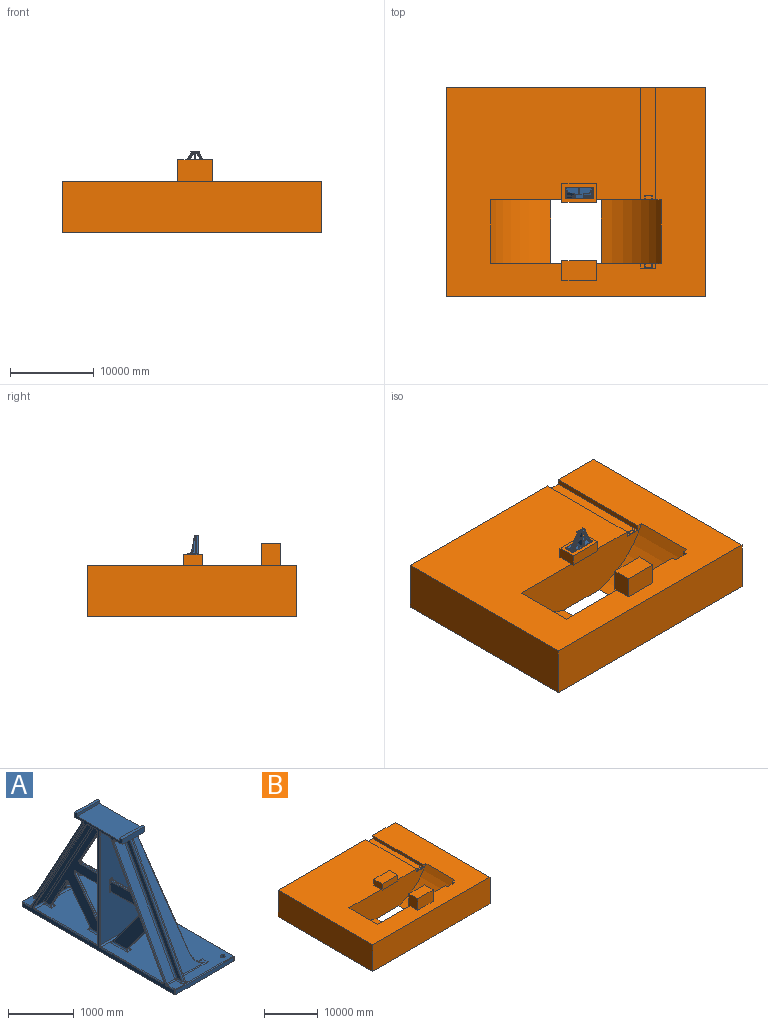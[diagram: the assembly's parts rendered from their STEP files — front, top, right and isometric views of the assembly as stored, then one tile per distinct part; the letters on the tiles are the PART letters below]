
ASSEMBLY  parts=2 mates=1
PART A: 292 faces, bbox 1283.8x3315.8x2337.9 mm
  f0: plane 2082.8x1322.33mm, normal (1,0,0), area 575527.7mm2, adj f52,f55,f57,f65,f122,f123,f124,f125
  f1: plane 2095.5x1322.33mm, normal (-1,0,0), area 576903.3mm2, adj f60,f62,f67,f78,f81,f82,f83,f84
  f2: plane 603.57x326.81mm, normal (0,0.88,-0.48), area 17433.8mm2, adj f58,f72,f98,f139
  f3: plane 3276.6x1244.6mm, normal (0,0,1), area 3608920.8mm2, adj f9,f30,f31,f35,f36,f38,f39,f42
  f4: plane 1020.58x474.48mm, normal (0,0,-1), area 273321.6mm2, adj f10,f12,f14,f29,f33,f41,f44,f45
  f5: plane 1244.6x76.2mm, normal (0,-1,0), area 94838.5mm2, adj f6,f103,f107,f108
  f6: plane 3302x1270mm, normal (0,0,-1), area 4184280.8mm2, adj f5,f7,f8,f103,f108,f150,f154,f244
  f7: plane 3276.6x76.2mm, normal (1,0,0), area 249676.9mm2, adj f6,f102,f103,f244
  f8: plane 3276.6x2324.1mm, normal (-1,0,0), area 478440.9mm2, adj f6,f13,f14,f15,f16,f101,f104,f106
  f9: cylinder r=457.2mm len=450.25mm, axis (0,1,0), area 36318.4mm2, adj f3,f10,f11,f70,f155,f212
  f10: plane 1757.68x311.48mm, normal (0.98,0,0.17), area 90851.4mm2, adj f4,f9,f11,f64,f155,f206
  f11: plane 2096.57x1067.85mm, normal (0,-1,0), area 1321127.4mm2, adj f9,f10,f64,f68,f70,f71,f85,f86
  f12: plane 1016x101.6mm, normal (1,0,0), area 56774.1mm2, adj f4,f13,f14,f15,f16,f156,f157,f158
  f13: plane 482.6x50.8mm, normal (0,0,1), area 24516.1mm2, adj f8,f12,f14,f16
  f14: plane 482.6x101.6mm, normal (0,-1,0), area 48997.5mm2, adj f4,f8,f12,f13,f101
  f15: plane 914.4x482.6mm, normal (0,0,1), area 441289.4mm2, adj f8,f12,f16,f158
  f16: plane 482.6x50.8mm, normal (0,1,0), area 24516.1mm2, adj f8,f12,f13,f15
  f17: plane 2083.01x1127.98mm, normal (0,-0.88,0.48), area 60174.3mm2, adj f19,f35,f38,f45,f46
  f18: plane 952.62x515.81mm, normal (0,0.88,-0.48), area 27546.8mm2, adj f50,f69,f81,f132,f133
  f19: plane 2082.8x1250.53mm, normal (1,0,0), area 255697.1mm2, adj f17,f34,f35,f41,f45
  f20: plane 2082.8x1221.65mm, normal (-1,0,0), area 195521.9mm2, adj f39,f43,f46,f49
  f21: plane 651.4x25.4mm, normal (0,0,-1), area 16545.6mm2, adj f71,f73,f89,f124
  f22: plane 546.03x25.4mm, normal (0,0,1), area 13869.1mm2, adj f68,f69,f83,f130
  f23: plane 869.61x653.2mm, normal (0,0.8,0.6), area 27764.6mm2, adj f73,f74,f91,f92,f121,f122
  f24: plane 603.57x453.37mm, normal (0,-0.8,-0.6), area 19173.9mm2, adj f66,f72,f96,f137
  f25: plane 2082.8x1127.77mm, normal (0,-0.88,0.48), area 421124.2mm2, adj f36,f43,f44,f106
  f26: plane 2082.8x1127.77mm, normal (0,0.88,-0.48), area 421124.2mm2, adj f59,f62,f63,f118
  f27: plane 2082.8x1127.77mm, normal (0,0.88,-0.48), area 592711.8mm2, adj f51,f54,f55,f143,f144
  f28: plane 2082.8x1127.77mm, normal (0,-0.88,0.48), area 604847.9mm2, adj f31,f33,f34,f147,f148
  f29: plane 1901.74x1059.44mm, normal (1,0,0.09), area 55530.4mm2, adj f4,f30,f142,f143,f148,f149
  f30: cylinder r=254mm len=253.03mm, axis (0,1,0), area 16525mm2, adj f3,f29,f144,f145,f146,f147
  f31: cylinder r=25.4mm len=588.35mm, axis (1,0,0), area 14676.3mm2, adj f3,f28,f32,f146
  f32: sphere r=25.4mm, area 494.1mm2, adj f31,f34,f35
  f33: cylinder r=25.4mm len=160mm, axis (1,0,0), area 8271.1mm2, adj f4,f28,f37,f149
  f34: cylinder r=25.4mm len=2094.89mm, axis (0,0.48,0.88), area 94500mm2, adj f19,f28,f32,f37
  f35: cylinder r=25.4mm len=151.64mm, axis (0,-1,0), area 5422.7mm2, adj f3,f17,f19,f32,f38
  f36: cylinder r=25.4mm len=177.8mm, axis (1,0,0), area 4852.7mm2, adj f3,f25,f40,f109
  f37: sphere r=25.4mm, area 1333.6mm2, adj f33,f34,f41
  f38: cylinder r=25.4mm len=50.8mm, axis (1,0,0), area 1081.7mm2, adj f3,f17,f35,f42
  f39: cylinder r=25.4mm len=93.87mm, axis (0,1,0), area 3745.4mm2, adj f3,f20,f40,f42
  f40: sphere r=25.4mm, area 640.7mm2, adj f36,f39,f43
  f41: cylinder r=25.4mm len=151.64mm, axis (0,1,0), area 5543.6mm2, adj f4,f19,f37,f45
  f42: bspline ~60.29x59.63mm, area 2051.8mm2, adj f3,f38,f39,f46
  f43: cylinder r=25.4mm len=2094.89mm, axis (0,-0.48,-0.88), area 94500mm2, adj f20,f25,f40,f47
  f44: cylinder r=25.4mm len=177.8mm, axis (1,0,0), area 9335.1mm2, adj f4,f25,f47,f104
  f45: cylinder r=25.4mm len=50.8mm, axis (1,0,0), area 1840.3mm2, adj f4,f17,f19,f41,f48
  f46: cylinder r=25.4mm len=2119.08mm, axis (0,0.48,0.88), area 94500mm2, adj f17,f20,f42,f48
  f47: sphere r=25.4mm, area 1333.6mm2, adj f43,f44,f49
  f48: bspline ~57.77x50.8mm, area 2732.6mm2, adj f4,f45,f46,f49
  f49: cylinder r=25.4mm len=93.87mm, axis (0,-1,0), area 3745.4mm2, adj f4,f20,f47,f48
  f50: cylinder r=25.4mm len=63.5mm, axis (1,0,0), area 1275.9mm2, adj f4,f18,f79,f134
  f51: cylinder r=25.4mm len=156.82mm, axis (1,0,0), area 4256.3mm2, adj f4,f27,f53,f142
  f52: cylinder r=25.4mm len=151.64mm, axis (0,1,0), area 5108.9mm2, adj f0,f4,f53,f133,f134
  f53: sphere r=25.4mm, area 494.1mm2, adj f51,f52,f55
  f54: cylinder r=25.4mm len=588.35mm, axis (1,0,0), area 26589.8mm2, adj f3,f27,f56,f145
  f55: cylinder r=25.4mm len=2094.89mm, axis (0,-0.48,-0.88), area 94500mm2, adj f0,f27,f53,f56
  f56: sphere r=25.4mm, area 1374.7mm2, adj f54,f55,f57
  f57: cylinder r=25.4mm len=151.64mm, axis (0,-1,0), area 5290.2mm2, adj f0,f3,f56,f141
  f58: cylinder r=25.4mm len=101.6mm, axis (1,0,0), area 2438.4mm2, adj f2,f3,f99,f100,f140,f141
  f59: cylinder r=25.4mm len=177.8mm, axis (1,0,0), area 9335.1mm2, adj f3,f26,f61,f116
  f60: cylinder r=25.4mm len=151.64mm, axis (0,1,0), area 5290.2mm2, adj f1,f3,f61,f100
  f61: sphere r=25.4mm, area 1292.5mm2, adj f59,f60,f62
  f62: cylinder r=25.4mm len=2107.59mm, axis (0,0.48,0.88), area 94813.9mm2, adj f1,f26,f61,f75,f76
  f63: cylinder r=25.4mm len=188.97mm, axis (1,0,0), area 5005.1mm2, adj f4,f26,f75,f119
  f64: cylinder r=25.4mm len=448.98mm, axis (-1,0,0), area 17824.1mm2, adj f4,f10,f11,f115
  f65: cylinder r=25.4mm len=378.52mm, axis (0,1,0), area 13151.4mm2, adj f0,f3,f70,f120,f121,f135
  f66: cylinder r=25.4mm len=101.6mm, axis (1,0,0), area 2949.2mm2, adj f3,f24,f94,f95,f135,f136
  f67: cylinder r=25.4mm len=378.52mm, axis (0,-1,0), area 13151.4mm2, adj f1,f3,f70,f92,f93,f94
  f68: cylinder r=25.4mm len=25.4mm, axis (1,0,0), area 1013.4mm2, adj f11,f22,f84,f129
  f69: cylinder r=25.4mm len=37.49mm, axis (-1,0,0), area 1333.6mm2, adj f18,f22,f82,f131
  f70: cylinder r=25.4mm len=1204.35mm, axis (1,0,0), area 44777.6mm2, adj f3,f9,f11,f65,f67,f74,f93,f112
  f71: cylinder r=25.4mm len=25.4mm, axis (-1,0,0), area 1013.4mm2, adj f11,f21,f88,f125
  f72: cylinder r=25.4mm len=42.64mm, axis (1,0,0), area 1291mm2, adj f2,f24,f97,f138
  f73: cylinder r=25.4mm len=40.66mm, axis (-1,0,0), area 1429mm2, adj f21,f23,f90,f123
  f74: cylinder r=25.4mm len=98.9mm, axis (-1,0,0), area 1579.5mm2, adj f23,f70,f93,f120
  f75: bspline ~23.3x22.79mm, area 176.2mm2, adj f62,f63,f76
  f76: bspline ~14.23x12.7mm, area 194.6mm2, adj f4,f62,f75,f78
  f77: bspline ~30.02x23.64mm, area 185.9mm2, adj f4,f79,f80
  f78: cylinder r=12.7mm len=108.32mm, axis (0,-1,0), area 2160.8mm2, adj f1,f4,f76,f80
  f79: torus R=38.1mm, axis (-1,0,0), area 200.7mm2, adj f50,f77,f81
  f80: bspline ~16.79x14.68mm, area 188.4mm2, adj f4,f77,f78,f81
  f81: cylinder r=12.7mm len=958.67mm, axis (0,-0.48,-0.88), area 21592.7mm2, adj f1,f18,f79,f80,f82
  f82: torus R=38.1mm, axis (-1,0,0), area 1237.7mm2, adj f1,f69,f81,f83
  f83: cylinder r=12.7mm len=546.03mm, axis (0,1,0), area 10892.8mm2, adj f1,f22,f82,f84
  f84: torus R=38.1mm, axis (-1,0,0), area 440.8mm2, adj f1,f68,f83,f85
  f85: bspline ~39.16x25.4mm, area 298.8mm2, adj f11,f84,f86
  f86: cylinder r=12.7mm len=188.72mm, axis (0,0,1), area 3764.9mm2, adj f1,f11,f85,f87
  f87: bspline ~39.16x25.4mm, area 270.9mm2, adj f11,f86,f88
  f88: torus R=38.1mm, axis (-1,0,0), area 440.9mm2, adj f1,f71,f87,f89
  f89: cylinder r=12.7mm len=651.4mm, axis (0,-1,0), area 12994.9mm2, adj f1,f21,f88,f90
  f90: torus R=38.1mm, axis (-1,0,0), area 1326.3mm2, adj f1,f73,f89,f91
  f91: cylinder r=12.7mm len=854.36mm, axis (0,0.6,-0.8), area 21126mm2, adj f1,f23,f90,f92
  f92: bspline ~33.54x31.13mm, area 456.3mm2, adj f23,f67,f91,f93
  f93: bspline ~29.74x29.74mm, area 282.5mm2, adj f67,f70,f74,f92
  f94: bspline ~38.1x38.1mm, area 343.6mm2, adj f66,f67,f95
  f95: torus R=38.1mm, axis (-1,0,0), area 385.7mm2, adj f1,f66,f94,f96
  f96: cylinder r=12.7mm len=611.2mm, axis (0,-0.6,0.8), area 15059.1mm2, adj f1,f24,f95,f97
  f97: torus R=38.1mm, axis (-1,0,0), area 1198.2mm2, adj f1,f72,f96,f98
  f98: cylinder r=12.7mm len=609.62mm, axis (0,-0.48,-0.88), area 13692.5mm2, adj f1,f2,f97,f99
  f99: torus R=38.1mm, axis (-1,0,0), area 297.2mm2, adj f1,f58,f98,f100
  f100: bspline ~38.1x38.1mm, area 343.5mm2, adj f58,f60,f99
  f101: cylinder r=12.7mm len=159.81mm, axis (0,1,0), area 3188mm2, adj f4,f8,f14,f104
  f102: cylinder r=12.7mm len=3276.6mm, axis (0,1,0), area 65365.3mm2, adj f3,f7,f105,f246
  f103: cylinder r=12.7mm len=76.2mm, axis (0,0,1), area 1520.1mm2, adj f5,f6,f7,f105
  f104: torus R=38.1mm, axis (1,0,0), area 1237.7mm2, adj f8,f44,f101,f106
  f105: sphere r=12.7mm, area 161.3mm2, adj f102,f103,f107
  f106: cylinder r=12.7mm len=2088.85mm, axis (0,-0.48,-0.88), area 47250mm2, adj f8,f25,f104,f109
  f107: cylinder r=12.7mm len=1244.6mm, axis (-1,0,0), area 24828.7mm2, adj f3,f5,f105,f110
  f108: cylinder r=12.7mm len=76.2mm, axis (0,0,-1), area 1520.1mm2, adj f5,f6,f8,f110
  f109: torus R=38.1mm, axis (1,0,0), area 643.4mm2, adj f8,f36,f106,f111
  f110: sphere r=12.7mm, area 345.4mm2, adj f107,f108,f111
  f111: cylinder r=12.7mm len=162.34mm, axis (0,-1,0), area 3238.4mm2, adj f3,f8,f109,f110
  f112: torus R=38.1mm, axis (1,0,0), area 940.5mm2, adj f8,f70,f113,f114
  f113: cylinder r=12.7mm len=2082.8mm, axis (0,0,1), area 41550mm2, adj f8,f11,f112,f115
  f114: cylinder r=12.7mm len=1309.63mm, axis (0,-1,0), area 26125.9mm2, adj f3,f8,f112,f116
  f115: torus R=38.1mm, axis (1,0,0), area 940.5mm2, adj f8,f64,f113,f117
  f116: torus R=38.1mm, axis (1,0,0), area 1237.7mm2, adj f8,f59,f114,f118
  f117: cylinder r=12.7mm len=181.86mm, axis (0,1,0), area 3627.9mm2, adj f4,f8,f115,f119
  f118: cylinder r=12.7mm len=2088.85mm, axis (0,0.48,0.88), area 47250mm2, adj f8,f26,f116,f119
  f119: torus R=38.1mm, axis (1,0,0), area 643.4mm2, adj f8,f63,f117,f118
  f120: bspline ~29.74x29.74mm, area 282.5mm2, adj f65,f70,f74,f121
  f121: bspline ~27.34x22.88mm, area 456.3mm2, adj f23,f65,f120,f122
  f122: cylinder r=12.7mm len=854.36mm, axis (0,-0.6,0.8), area 21126mm2, adj f0,f23,f121,f123
  f123: torus R=38.1mm, axis (-1,0,0), area 1326.3mm2, adj f0,f73,f122,f124
  f124: cylinder r=12.7mm len=651.4mm, axis (0,1,0), area 12994.9mm2, adj f0,f21,f123,f125
  f125: torus R=38.1mm, axis (-1,0,0), area 440.9mm2, adj f0,f71,f124,f126
  f126: bspline ~39.16x25.4mm, area 298.8mm2, adj f11,f125,f127
  f127: cylinder r=12.7mm len=188.72mm, axis (0,0,-1), area 3764.9mm2, adj f0,f11,f126,f128
  f128: bspline ~39.16x25.4mm, area 270.9mm2, adj f11,f127,f129
  f129: torus R=38.1mm, axis (-1,0,0), area 440.8mm2, adj f0,f68,f128,f130
  f130: cylinder r=12.7mm len=546.03mm, axis (0,-1,0), area 10892.8mm2, adj f0,f22,f129,f131
  f131: torus R=38.1mm, axis (-1,0,0), area 1237.7mm2, adj f0,f69,f130,f132
  f132: cylinder r=12.7mm len=940.53mm, axis (0,0.48,0.88), area 21199.5mm2, adj f0,f18,f131,f133
  f133: bspline ~20.99x18.14mm, area 330.5mm2, adj f18,f52,f132,f134
  f134: bspline ~34.19x34.19mm, area 223.5mm2, adj f50,f52,f133
  f135: bspline ~38.1x38.1mm, area 343.6mm2, adj f65,f66,f136
  f136: torus R=38.1mm, axis (-1,0,0), area 385.7mm2, adj f0,f66,f135,f137
  f137: cylinder r=12.7mm len=611.2mm, axis (0,0.6,-0.8), area 15059.1mm2, adj f0,f24,f136,f138
  f138: torus R=38.1mm, axis (-1,0,0), area 1198.2mm2, adj f0,f72,f137,f139
  f139: cylinder r=12.7mm len=609.62mm, axis (0,0.48,0.88), area 13692.5mm2, adj f0,f2,f138,f140
  f140: torus R=38.1mm, axis (-1,0,0), area 297.2mm2, adj f0,f58,f139,f141
  f141: bspline ~38.1x38.1mm, area 343.5mm2, adj f57,f58,f140
  f142: bspline ~33.5x27.11mm, area 374.1mm2, adj f4,f29,f51,f143
  f143: cylinder r=12.7mm len=1902.74mm, axis (-0.08,0.47,0.88), area 44269.8mm2, adj f27,f29,f142,f144
  f144: bspline ~194.37x112.54mm, area 5355mm2, adj f27,f30,f143,f145
  f145: bspline ~168.55x57.15mm, area 1354.2mm2, adj f30,f54,f144
  f146: bspline ~111.26x35.53mm, area 484.5mm2, adj f30,f31,f147
  f147: bspline ~223.5x169.28mm, area 5116.1mm2, adj f28,f30,f146,f148
  f148: cylinder r=12.7mm len=1864.3mm, axis (0.08,-0.47,-0.88), area 41186.5mm2, adj f28,f29,f147,f149
  f149: bspline ~56.24x38.1mm, area 971.6mm2, adj f4,f29,f33,f148
  f150: cylinder r=38.1mm len=88.9mm, axis (0,0,1), area 21281.7mm2, adj f3,f6
  f151: plane 2082.8x1322.33mm, normal (1,0,0), area 575527.7mm2, adj f194,f197,f199,f207,f263,f264,f265,f266
  f152: plane 2095.5x1322.33mm, normal (-1,0,0), area 576903.3mm2, adj f202,f204,f209,f220,f223,f224,f225,f226
  f153: plane 603.57x326.81mm, normal (0,-0.88,-0.48), area 17433.8mm2, adj f200,f214,f240,f280
  f154: plane 1244.6x76.2mm, normal (0,1,0), area 94838.5mm2, adj f6,f244,f248,f249
  f155: plane 2096.57x1067.85mm, normal (0,1,0), area 1321127.4mm2, adj f9,f10,f206,f210,f212,f213,f227,f228
  f156: plane 482.6x50.8mm, normal (0,0,1), area 24516.1mm2, adj f8,f12,f157,f158
  f157: plane 482.6x101.6mm, normal (0,1,0), area 48997.5mm2, adj f4,f8,f12,f156,f243
  f158: plane 482.6x50.8mm, normal (0,-1,0), area 24516.1mm2, adj f8,f12,f15,f156
  f159: plane 2083.01x1127.98mm, normal (0,0.88,0.48), area 60174.3mm2, adj f161,f177,f180,f187,f188
  f160: plane 952.62x515.81mm, normal (0,-0.88,-0.48), area 27546.8mm2, adj f192,f211,f223,f273,f274
  f161: plane 2082.8x1250.53mm, normal (1,0,0), area 255697.1mm2, adj f159,f176,f177,f183,f187
  f162: plane 2082.8x1221.65mm, normal (-1,0,0), area 195521.9mm2, adj f181,f185,f188,f191
  f163: plane 651.4x25.4mm, normal (0,0,-1), area 16545.6mm2, adj f213,f215,f231,f265
  f164: plane 546.03x25.4mm, normal (0,0,1), area 13869.1mm2, adj f210,f211,f225,f271
  f165: plane 869.61x653.2mm, normal (0,-0.8,0.6), area 27764.6mm2, adj f215,f216,f233,f234,f262,f263
  f166: plane 603.57x453.37mm, normal (0,0.8,-0.6), area 19173.9mm2, adj f208,f214,f238,f278
  f167: plane 2082.8x1127.77mm, normal (0,0.88,0.48), area 421124.2mm2, adj f178,f185,f186,f247
  f168: plane 2082.8x1127.77mm, normal (0,-0.88,-0.48), area 421124.2mm2, adj f201,f204,f205,f259
  f169: plane 2082.8x1127.77mm, normal (0,-0.88,-0.48), area 592711.8mm2, adj f193,f196,f197,f284,f285
  f170: plane 2082.8x1127.77mm, normal (0,0.88,0.48), area 604847.9mm2, adj f173,f175,f176,f288,f289
  f171: plane 1901.74x1059.44mm, normal (1,0,0.09), area 55530.4mm2, adj f4,f172,f283,f284,f289,f290
  f172: cylinder r=254mm len=253.03mm, axis (0,-1,0), area 16525mm2, adj f3,f171,f285,f286,f287,f288
  f173: cylinder r=25.4mm len=588.35mm, axis (1,0,0), area 14676.3mm2, adj f3,f170,f174,f287
  f174: sphere r=25.4mm, area 494.1mm2, adj f173,f176,f177
  f175: cylinder r=25.4mm len=160mm, axis (1,0,0), area 8271.1mm2, adj f4,f170,f179,f290
  f176: cylinder r=25.4mm len=2094.89mm, axis (0,-0.48,0.88), area 94500mm2, adj f161,f170,f174,f179
  f177: cylinder r=25.4mm len=151.64mm, axis (0,1,0), area 5422.7mm2, adj f3,f159,f161,f174,f180
  f178: cylinder r=25.4mm len=177.8mm, axis (1,0,0), area 4852.7mm2, adj f3,f167,f182,f250
  f179: sphere r=25.4mm, area 1374.7mm2, adj f175,f176,f183
  f180: cylinder r=25.4mm len=50.8mm, axis (1,0,0), area 1081.7mm2, adj f3,f159,f177,f184
  f181: cylinder r=25.4mm len=93.87mm, axis (0,-1,0), area 3745.4mm2, adj f3,f162,f182,f184
  f182: sphere r=25.4mm, area 494.1mm2, adj f178,f181,f185
  f183: cylinder r=25.4mm len=151.64mm, axis (0,-1,0), area 5543.6mm2, adj f4,f161,f179,f187
  f184: bspline ~60.29x59.63mm, area 2051.8mm2, adj f3,f180,f181,f188
  f185: cylinder r=25.4mm len=2094.89mm, axis (0,0.48,-0.88), area 94500mm2, adj f162,f167,f182,f189
  f186: cylinder r=25.4mm len=177.8mm, axis (1,0,0), area 9335.1mm2, adj f4,f167,f189,f245
  f187: cylinder r=25.4mm len=50.8mm, axis (1,0,0), area 1840.3mm2, adj f4,f159,f161,f183,f190
  f188: cylinder r=25.4mm len=2119.08mm, axis (0,-0.48,0.88), area 94500mm2, adj f159,f162,f184,f190
  f189: sphere r=25.4mm, area 1292.5mm2, adj f185,f186,f191
  f190: bspline ~57.77x50.8mm, area 2732.6mm2, adj f4,f187,f188,f191
  f191: cylinder r=25.4mm len=93.87mm, axis (0,1,0), area 3745.4mm2, adj f4,f162,f189,f190
  f192: cylinder r=25.4mm len=63.5mm, axis (1,0,0), area 1275.9mm2, adj f4,f160,f221,f275
  f193: cylinder r=25.4mm len=156.82mm, axis (1,0,0), area 4256.3mm2, adj f4,f169,f195,f283
  f194: cylinder r=25.4mm len=151.64mm, axis (0,-1,0), area 5108.9mm2, adj f4,f151,f195,f274,f275
  f195: sphere r=25.4mm, area 494.1mm2, adj f193,f194,f197
  f196: cylinder r=25.4mm len=588.35mm, axis (1,0,0), area 26589.8mm2, adj f3,f169,f198,f286
  f197: cylinder r=25.4mm len=2094.89mm, axis (0,0.48,-0.88), area 94500mm2, adj f151,f169,f195,f198
  f198: sphere r=25.4mm, area 1333.6mm2, adj f196,f197,f199
  f199: cylinder r=25.4mm len=151.64mm, axis (0,1,0), area 5290.2mm2, adj f3,f151,f198,f282
  f200: cylinder r=25.4mm len=101.6mm, axis (1,0,0), area 2438.4mm2, adj f3,f153,f241,f242,f281,f282
  f201: cylinder r=25.4mm len=177.8mm, axis (1,0,0), area 9335.1mm2, adj f3,f168,f203,f257
  f202: cylinder r=25.4mm len=151.64mm, axis (0,-1,0), area 5290.2mm2, adj f3,f152,f203,f242
  f203: sphere r=25.4mm, area 1333.6mm2, adj f201,f202,f204
  f204: cylinder r=25.4mm len=2107.59mm, axis (0,-0.48,0.88), area 94813.9mm2, adj f152,f168,f203,f217,f218
  f205: cylinder r=25.4mm len=188.97mm, axis (1,0,0), area 5005.1mm2, adj f4,f168,f217,f260
  f206: cylinder r=25.4mm len=448.98mm, axis (-1,0,0), area 17824.1mm2, adj f4,f10,f155,f256
  f207: cylinder r=25.4mm len=378.52mm, axis (0,-1,0), area 13151.4mm2, adj f3,f151,f212,f261,f262,f276
  f208: cylinder r=25.4mm len=101.6mm, axis (1,0,0), area 2949.2mm2, adj f3,f166,f236,f237,f276,f277
  f209: cylinder r=25.4mm len=378.52mm, axis (0,1,0), area 13151.4mm2, adj f3,f152,f212,f234,f235,f236
  f210: cylinder r=25.4mm len=25.4mm, axis (1,0,0), area 1013.4mm2, adj f155,f164,f226,f270
  f211: cylinder r=25.4mm len=37.49mm, axis (-1,0,0), area 1333.6mm2, adj f160,f164,f224,f272
  f212: cylinder r=25.4mm len=1204.35mm, axis (1,0,0), area 44777.6mm2, adj f3,f9,f155,f207,f209,f216,f235,f253
  f213: cylinder r=25.4mm len=25.4mm, axis (-1,0,0), area 1013.4mm2, adj f155,f163,f230,f266
  f214: cylinder r=25.4mm len=42.64mm, axis (1,0,0), area 1291mm2, adj f153,f166,f239,f279
  f215: cylinder r=25.4mm len=40.66mm, axis (-1,0,0), area 1429mm2, adj f163,f165,f232,f264
  f216: cylinder r=25.4mm len=98.9mm, axis (-1,0,0), area 1579.5mm2, adj f165,f212,f235,f261
  f217: bspline ~23.3x22.79mm, area 176.2mm2, adj f204,f205,f218
  f218: bspline ~14.23x12.7mm, area 194.6mm2, adj f4,f204,f217,f220
  f219: bspline ~32.05x24.65mm, area 185.9mm2, adj f4,f221,f222
  f220: cylinder r=12.7mm len=108.32mm, axis (0,1,0), area 2160.8mm2, adj f4,f152,f218,f222
  f221: torus R=38.1mm, axis (-1,0,0), area 200.7mm2, adj f192,f219,f223
  f222: bspline ~16.79x14.68mm, area 188.4mm2, adj f4,f219,f220,f223
  f223: cylinder r=12.7mm len=958.67mm, axis (0,0.48,-0.88), area 21592.7mm2, adj f152,f160,f221,f222,f224
  f224: torus R=38.1mm, axis (-1,0,0), area 1237.7mm2, adj f152,f211,f223,f225
  f225: cylinder r=12.7mm len=546.03mm, axis (0,-1,0), area 10892.8mm2, adj f152,f164,f224,f226
  f226: torus R=38.1mm, axis (-1,0,0), area 440.9mm2, adj f152,f210,f225,f227
  f227: bspline ~39.16x25.4mm, area 270.9mm2, adj f155,f226,f228
  f228: cylinder r=12.7mm len=188.72mm, axis (0,0,1), area 3764.9mm2, adj f152,f155,f227,f229
  f229: bspline ~39.16x25.4mm, area 298.8mm2, adj f155,f228,f230
  f230: torus R=38.1mm, axis (-1,0,0), area 440.8mm2, adj f152,f213,f229,f231
  f231: cylinder r=12.7mm len=651.4mm, axis (0,1,0), area 12994.9mm2, adj f152,f163,f230,f232
  f232: torus R=38.1mm, axis (-1,0,0), area 1326.3mm2, adj f152,f215,f231,f233
  f233: cylinder r=12.7mm len=854.36mm, axis (0,-0.6,-0.8), area 21126mm2, adj f152,f165,f232,f234
  f234: bspline ~33.54x31.13mm, area 456.3mm2, adj f165,f209,f233,f235
  f235: bspline ~29.74x29.74mm, area 282.5mm2, adj f209,f212,f216,f234
  f236: bspline ~38.1x38.1mm, area 343.6mm2, adj f208,f209,f237
  f237: torus R=38.1mm, axis (-1,0,0), area 385.7mm2, adj f152,f208,f236,f238
  f238: cylinder r=12.7mm len=611.2mm, axis (0,0.6,0.8), area 15059.1mm2, adj f152,f166,f237,f239
  f239: torus R=38.1mm, axis (-1,0,0), area 1198.2mm2, adj f152,f214,f238,f240
  f240: cylinder r=12.7mm len=609.62mm, axis (0,0.48,-0.88), area 13692.5mm2, adj f152,f153,f239,f241
  f241: torus R=38.1mm, axis (-1,0,0), area 297.2mm2, adj f152,f200,f240,f242
  f242: bspline ~38.1x38.1mm, area 343.5mm2, adj f200,f202,f241
  f243: cylinder r=12.7mm len=159.81mm, axis (0,-1,0), area 3188mm2, adj f4,f8,f157,f245
  f244: cylinder r=12.7mm len=76.2mm, axis (0,0,1), area 1520.1mm2, adj f6,f7,f154,f246
  f245: torus R=38.1mm, axis (1,0,0), area 1237.7mm2, adj f8,f186,f243,f247
  f246: sphere r=12.7mm, area 253.4mm2, adj f102,f244,f248
  f247: cylinder r=12.7mm len=2088.85mm, axis (0,0.48,-0.88), area 47250mm2, adj f8,f167,f245,f250
  f248: cylinder r=12.7mm len=1244.6mm, axis (-1,0,0), area 24828.7mm2, adj f3,f154,f246,f251
  f249: cylinder r=12.7mm len=76.2mm, axis (0,0,-1), area 1520.1mm2, adj f6,f8,f154,f251
  f250: torus R=38.1mm, axis (1,0,0), area 643.4mm2, adj f8,f178,f247,f252
  f251: sphere r=12.7mm, area 253.4mm2, adj f248,f249,f252
  f252: cylinder r=12.7mm len=162.34mm, axis (0,1,0), area 3238.4mm2, adj f3,f8,f250,f251
  f253: torus R=38.1mm, axis (1,0,0), area 940.5mm2, adj f8,f212,f254,f255
  f254: cylinder r=12.7mm len=2082.8mm, axis (0,0,1), area 41550mm2, adj f8,f155,f253,f256
  f255: cylinder r=12.7mm len=1309.63mm, axis (0,1,0), area 26125.9mm2, adj f3,f8,f253,f257
  f256: torus R=38.1mm, axis (1,0,0), area 940.5mm2, adj f8,f206,f254,f258
  f257: torus R=38.1mm, axis (1,0,0), area 1237.7mm2, adj f8,f201,f255,f259
  f258: cylinder r=12.7mm len=181.86mm, axis (0,-1,0), area 3627.9mm2, adj f4,f8,f256,f260
  f259: cylinder r=12.7mm len=2088.85mm, axis (0,-0.48,0.88), area 47250mm2, adj f8,f168,f257,f260
  f260: torus R=38.1mm, axis (1,0,0), area 643.4mm2, adj f8,f205,f258,f259
  f261: bspline ~29.74x29.74mm, area 282.5mm2, adj f207,f212,f216,f262
  f262: bspline ~27.34x22.88mm, area 456.3mm2, adj f165,f207,f261,f263
  f263: cylinder r=12.7mm len=854.36mm, axis (0,0.6,0.8), area 21126mm2, adj f151,f165,f262,f264
  f264: torus R=38.1mm, axis (-1,0,0), area 1326.3mm2, adj f151,f215,f263,f265
  f265: cylinder r=12.7mm len=651.4mm, axis (0,-1,0), area 12994.9mm2, adj f151,f163,f264,f266
  f266: torus R=38.1mm, axis (-1,0,0), area 440.8mm2, adj f151,f213,f265,f267
  f267: bspline ~39.16x25.4mm, area 270.9mm2, adj f155,f266,f268
  f268: cylinder r=12.7mm len=188.72mm, axis (0,0,-1), area 3764.9mm2, adj f151,f155,f267,f269
  f269: bspline ~39.16x25.4mm, area 298.8mm2, adj f155,f268,f270
  f270: torus R=38.1mm, axis (-1,0,0), area 440.9mm2, adj f151,f210,f269,f271
  f271: cylinder r=12.7mm len=546.03mm, axis (0,1,0), area 10892.8mm2, adj f151,f164,f270,f272
  f272: torus R=38.1mm, axis (-1,0,0), area 1237.7mm2, adj f151,f211,f271,f273
  f273: cylinder r=12.7mm len=940.53mm, axis (0,-0.48,0.88), area 21199.5mm2, adj f151,f160,f272,f274
  f274: bspline ~20.99x18.14mm, area 330.5mm2, adj f160,f194,f273,f275
  f275: bspline ~34.19x34.19mm, area 223.5mm2, adj f192,f194,f274
  f276: bspline ~38.1x38.1mm, area 343.6mm2, adj f207,f208,f277
  f277: torus R=38.1mm, axis (-1,0,0), area 385.7mm2, adj f151,f208,f276,f278
  f278: cylinder r=12.7mm len=611.2mm, axis (0,-0.6,-0.8), area 15059.1mm2, adj f151,f166,f277,f279
  f279: torus R=38.1mm, axis (-1,0,0), area 1198.2mm2, adj f151,f214,f278,f280
  f280: cylinder r=12.7mm len=609.62mm, axis (0,-0.48,0.88), area 13692.5mm2, adj f151,f153,f279,f281
  f281: torus R=38.1mm, axis (-1,0,0), area 297.2mm2, adj f151,f200,f280,f282
  f282: bspline ~38.1x38.1mm, area 343.5mm2, adj f199,f200,f281
  f283: bspline ~33.5x27.11mm, area 374.1mm2, adj f4,f171,f193,f284
  f284: cylinder r=12.7mm len=1902.74mm, axis (-0.08,-0.47,0.88), area 44269.8mm2, adj f169,f171,f283,f285
  f285: bspline ~194.37x112.54mm, area 5355mm2, adj f169,f172,f284,f286
  f286: bspline ~168.55x57.15mm, area 1346.7mm2, adj f172,f196,f285
  f287: bspline ~101.23x33.5mm, area 484.5mm2, adj f172,f173,f288
  f288: bspline ~223.5x169.28mm, area 5116.1mm2, adj f170,f172,f287,f289
  f289: cylinder r=12.7mm len=1864.3mm, axis (0.08,0.47,-0.88), area 41186.5mm2, adj f170,f171,f288,f290
  f290: bspline ~56.24x38.1mm, area 971.6mm2, adj f4,f171,f175,f289
  f291: cylinder r=38.1mm len=88.9mm, axis (0,0,1), area 21281.7mm2, adj f3,f6
PART B: 71 faces, bbox 30939x25003.1x8724.9 mm
  f0: plane 914.4x444.5mm, normal (0,0,1), area 397789.7mm2, adj f51,f52,f53,f54,f55,f56,f57,f58
  f1: plane 914.4x444.5mm, normal (0,0,1), area 397789.7mm2, adj f31,f32,f33,f34,f35,f36,f37,f38
  f2: plane 20320x6096mm, normal (0,-1,0), area 92135743.4mm2, adj f4,f8,f15,f25,f26,f27,f29,f30
  f3: plane 20320x6096mm, normal (0,1,0), area 92135743.4mm2, adj f4,f8,f14,f21,f22,f23,f29,f30
  f4: plane 30938.97x25003.13mm, normal (0,0,1), area 577332546.4mm2, adj f2,f3,f5,f6,f7,f9,f10,f11
  f5: plane 25003.13x6096mm, normal (-1,0,0), area 152419063.8mm2, adj f4,f7,f8,f28
  f6: plane 25003.13x6096mm, normal (1,0,0), area 152419063.8mm2, adj f4,f7,f8,f28
  f7: plane 30938.97x6096mm, normal (0,-1,0), area 188603967mm2, adj f4,f5,f6,f8
  f8: plane 30938.97x25003.13mm, normal (0,0,-1), area 728019097.3mm2, adj f2,f3,f5,f6,f7,f28,f29,f30
  f9: plane 2628.9x2306.43mm, normal (-1,0,0), area 6063385.9mm2, adj f4,f10,f12,f13,f14
  f10: plane 4114.8x2628.9mm, normal (0,-1,0), area 10817397.7mm2, adj f4,f9,f11,f13
  f11: plane 2628.9x2306.43mm, normal (1,0,0), area 6063385.9mm2, adj f4,f10,f12,f13,f14
  f12: plane 4114.8x2628.9mm, normal (0,1,0), area 10817397.7mm2, adj f9,f11,f13,f14
  f13: plane 4114.8x2306.43mm, normal (0,0,1), area 9490517mm2, adj f9,f10,f11,f12
  f14: plane 4114.8x304.8mm, normal (0,0,-1), area 1254191mm2, adj f3,f9,f11,f12
  f15: plane 4114.8x304.8mm, normal (0,0,-1), area 1254191mm2, adj f2,f16,f17,f18
  f16: plane 2236.64x1333.5mm, normal (-1,0,0), area 2982555.6mm2, adj f4,f15,f17,f19,f20
  f17: plane 4114.8x1333.5mm, normal (0,-1,0), area 5487085.8mm2, adj f15,f16,f18,f20
  f18: plane 2236.64x1333.5mm, normal (1,0,0), area 2982555.6mm2, adj f4,f15,f17,f19,f20
  f19: plane 4114.8x1333.5mm, normal (0,1,0), area 5487085.8mm2, adj f4,f16,f18,f20
  f20: plane 4114.8x2236.64mm, normal (0,0,1), area 9203314.4mm2, adj f16,f17,f18,f19
  f21: plane 1806.46x542.11mm, normal (0,0,1), area 513056.1mm2, adj f3,f22,f23,f24,f51,f52,f53,f54
  f22: plane 647.7x542.11mm, normal (1,0,0), area 351124.7mm2, adj f3,f4,f21,f24
  f23: plane 647.7x542.11mm, normal (-1,0,0), area 351124.7mm2, adj f3,f4,f21,f24
  f24: plane 1806.46x647.7mm, normal (0,1,0), area 1170040.9mm2, adj f4,f21,f22,f23
  f25: plane 13415.96x647.7mm, normal (-1,0,0), area 8689519.6mm2, adj f2,f4,f27,f28
  f26: plane 13415.96x647.7mm, normal (1,0,0), area 8689519.6mm2, adj f2,f4,f27,f28
  f27: plane 13415.96x1806.46mm, normal (0,0,1), area 23769093.7mm2, adj f2,f25,f26,f28,f31,f32,f33,f34
  f28: plane 30938.97x6096mm, normal (0,1,0), area 187433926.1mm2, adj f4,f5,f6,f8,f25,f26,f27
  f29: cylinder r=11188.53mm len=7620mm, axis (0,1,0), area 74022255mm2, adj f2,f3,f4,f8
  f30: cylinder r=11188.53mm len=7620mm, axis (0,1,0), area 74022255mm2, adj f2,f3,f4,f8
  f31: cone r=25.4mm half-angle=30deg, axis (0,0,-1), area 2515.3mm2, adj f1,f27,f32,f38
  f32: plane 393.7x38.1mm, normal (-0.87,0,0.5), area 17320.5mm2, adj f1,f27,f31,f33
  f33: cone r=25.4mm half-angle=30deg, axis (0,0,-1), area 2515.3mm2, adj f1,f27,f32,f34
  f34: plane 863.6x38.1mm, normal (0,0.87,0.5), area 37993.3mm2, adj f1,f27,f33,f35
  f35: cone r=25.4mm half-angle=30deg, axis (0,0,-1), area 2515.3mm2, adj f1,f27,f34,f36
  f36: plane 393.7x38.1mm, normal (0.87,0,0.5), area 17320.5mm2, adj f1,f27,f35,f37
  f37: cone r=25.4mm half-angle=30deg, axis (0,0,-1), area 2515.3mm2, adj f1,f27,f36,f38
  f38: plane 863.6x38.1mm, normal (0,-0.87,0.5), area 37993.3mm2, adj f1,f27,f31,f37
  f39: cylinder r=25.4mm len=171.45mm, axis (0,0,-1), area 27362.2mm2, adj f1,f48
  f40: plane 38.1x38.1mm, normal (0,0,1), area 1140.1mm2, adj f48
  f41: cylinder r=25.4mm len=171.45mm, axis (0,0,-1), area 27362.2mm2, adj f1,f47
  f42: plane 38.1x38.1mm, normal (0,0,1), area 1140.1mm2, adj f47
  f43: cylinder r=25.4mm len=171.45mm, axis (0,0,-1), area 27362.2mm2, adj f1,f50
  f44: plane 38.1x38.1mm, normal (0,0,1), area 1140.1mm2, adj f50
  f45: cylinder r=25.4mm len=171.45mm, axis (0,0,-1), area 27362.2mm2, adj f1,f49
  f46: plane 38.1x38.1mm, normal (0,0,1), area 1140.1mm2, adj f49
  f47: cone r=19.05mm half-angle=45deg, axis (0,0,-1), area 1254mm2, adj f41,f42
  f48: cone r=19.05mm half-angle=45deg, axis (0,0,-1), area 1254mm2, adj f39,f40
  f49: cone r=19.05mm half-angle=45deg, axis (0,0,-1), area 1254mm2, adj f45,f46
  f50: cone r=19.05mm half-angle=45deg, axis (0,0,-1), area 1254mm2, adj f43,f44
  f51: cone r=25.4mm half-angle=30deg, axis (0,0,-1), area 2515.3mm2, adj f0,f21,f52,f58
  f52: plane 393.7x38.1mm, normal (-0.87,0,0.5), area 17320.5mm2, adj f0,f21,f51,f53
  f53: cone r=25.4mm half-angle=30deg, axis (0,0,-1), area 2515.3mm2, adj f0,f21,f52,f54
  f54: plane 863.6x38.1mm, normal (0,0.87,0.5), area 37993.3mm2, adj f0,f21,f53,f55
  f55: cone r=25.4mm half-angle=30deg, axis (0,0,-1), area 2515.3mm2, adj f0,f21,f54,f56
  f56: plane 393.7x38.1mm, normal (0.87,0,0.5), area 17320.5mm2, adj f0,f21,f55,f57
  f57: cone r=25.4mm half-angle=30deg, axis (0,0,-1), area 2515.3mm2, adj f0,f21,f56,f58
  f58: plane 863.6x38.1mm, normal (0,-0.87,0.5), area 37993.3mm2, adj f0,f21,f51,f57
  f59: cylinder r=25.4mm len=171.45mm, axis (0,0,-1), area 27362.2mm2, adj f0,f68
  f60: plane 38.1x38.1mm, normal (0,0,1), area 1140.1mm2, adj f68
  f61: cylinder r=25.4mm len=171.45mm, axis (0,0,-1), area 27362.2mm2, adj f0,f67
  f62: plane 38.1x38.1mm, normal (0,0,1), area 1140.1mm2, adj f67
  f63: cylinder r=25.4mm len=171.45mm, axis (0,0,-1), area 27362.2mm2, adj f0,f70
  f64: plane 38.1x38.1mm, normal (0,0,1), area 1140.1mm2, adj f70
  f65: cylinder r=25.4mm len=171.45mm, axis (0,0,-1), area 27362.2mm2, adj f0,f69
  f66: plane 38.1x38.1mm, normal (0,0,1), area 1140.1mm2, adj f69
  f67: cone r=19.05mm half-angle=45deg, axis (0,0,-1), area 1254mm2, adj f61,f62
  f68: cone r=19.05mm half-angle=45deg, axis (0,0,-1), area 1254mm2, adj f59,f60
  f69: cone r=19.05mm half-angle=45deg, axis (0,0,-1), area 1254mm2, adj f65,f66
  f70: cone r=19.05mm half-angle=45deg, axis (0,0,-1), area 1254mm2, adj f63,f64
PLACE A rot(axis=(0,0,1),90deg) t=(377.3,3989.63,1333.5)mm
PLACE B at identity fixed
MATE fastened A.f6 <-> B.f20  axis (0,0,-1) through (377.3,4623.52,1333.5)mm
